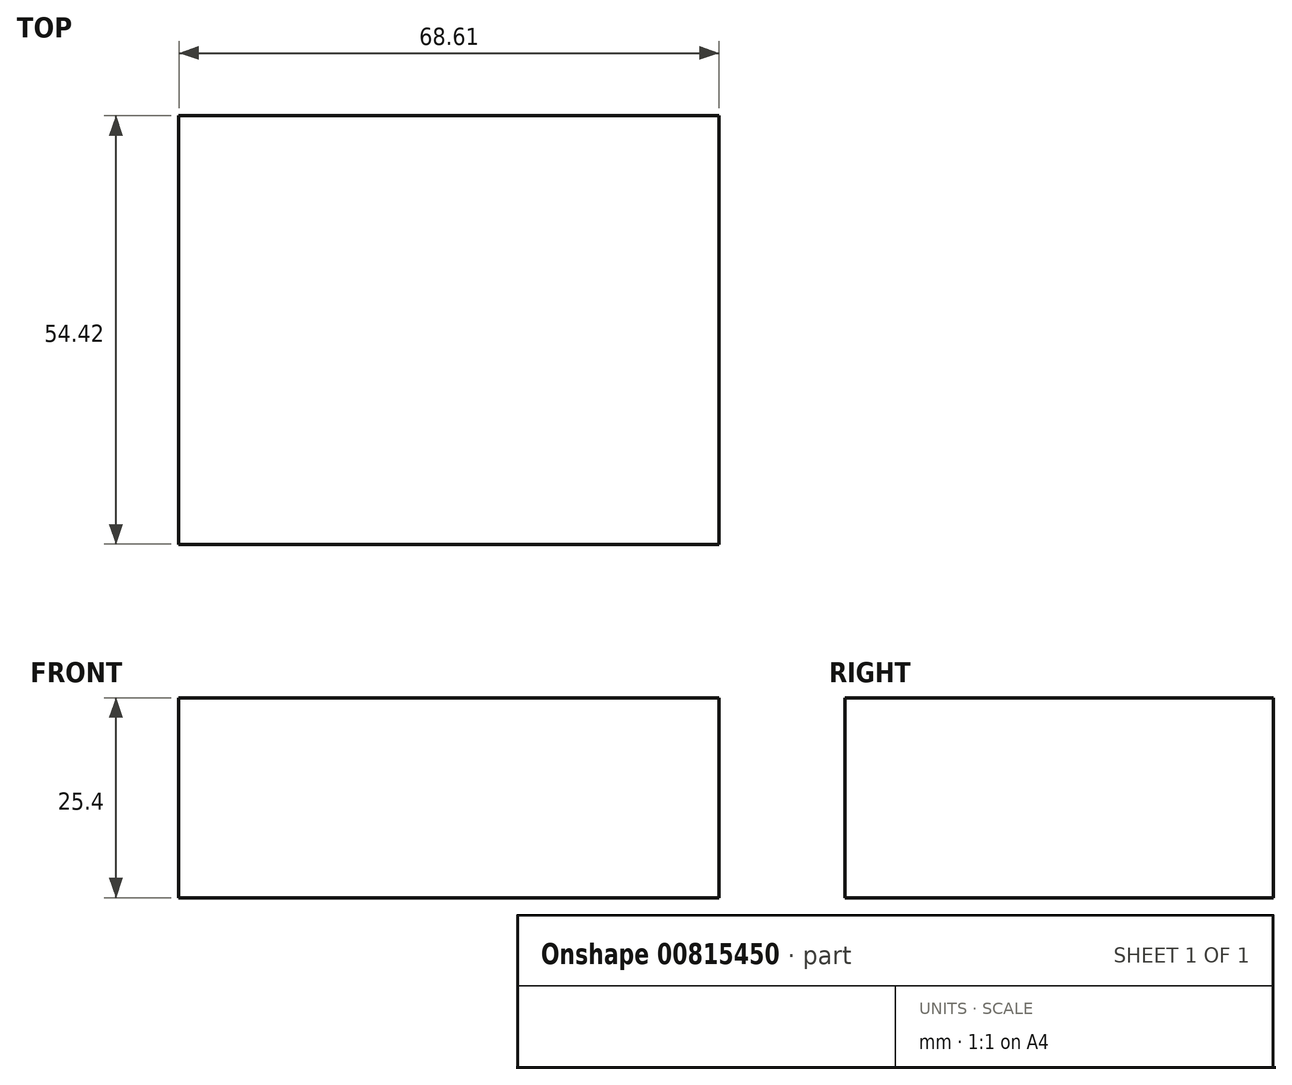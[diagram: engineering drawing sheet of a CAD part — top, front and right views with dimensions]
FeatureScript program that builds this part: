
annotation { "Feature Type Name" : "Feature", "Feature Type Description" : "" }
export const myFeature = defineFeature(function(context is Context, id is Id, definition is map)
    precondition{}
    {
        {
            var Q0;
            Q0=qCreatedBy(makeId("Top.planeOp"),FACE);
            var sketch = newSketch(context, id + "F0", { "sketchPlane" : qUnion([Q0])});
            skLineSegment(sketch, "E0.bottom", {"start": v(-32.8, -31.98) * mm, "end": v(35.82, -31.98) * mm});
            skLineSegment(sketch, "E0.top", {"start": v(-32.8, 22.44) * mm, "end": v(35.82, 22.44) * mm});
            skLineSegment(sketch, "E0.left", {"start": v(-32.8, -31.98) * mm, "end": v(-32.8, 22.44) * mm});
            skLineSegment(sketch, "E0.right", {"start": v(35.82, -31.98) * mm, "end": v(35.82, 22.44) * mm});
            skSolve(sketch);
        }
        {
            var Q0;
            Q0=makeQuery(id+"F0.imprint","IMPRINT",FACE,{"disambiguationData":[TD([[makeQuery(id+"F0.imprint","IMPRINT",EDGE,{"derivedFrom":sQuery(id+"F0.wireOp",EDGE,"E0.bottom")}),1.0]])]});
            extrude(context, id + "F1", {"entities" : qUnion([Q0]), "depth" : 25.4 * mm, "offsetDistance" : 25.4 * mm});
        }
    });
